# Revit family: HOSPITAIR C 15 bar
name_source: partatom
category: Equipement de génie climatique
revit_build: Autodesk Revit 2018 (Build: 20170223_1515(x64)
units: mm (PartAtom-declared; Revit-internal decimal feet)

## family parameters
Basée sur le plan de construction = Non
Classification = Aucun
Cote de connecteur circulaire = Utiliser le diamètre
Couper avec des vides une fois chargée = Non
Partagée = Non
Point de calcul de pièce = Non
Toujours verticalement = Oui
Type d'élément = Normal

## types (21) — shared parameters
BRANCHEMENT_TERRE = Oui
COS_PHI = 0.9
DESCR_CONDENSAT = Refoulement Condensat; Douille cannelée G1/2"
DIAM_REFOUL_CONDENSAT = 14 mm  [stored 0.0459318 ft]
Debit_refoulement_condensat = 0.0 m³/h
ELEC_ALIM X = Oui
HAUTEUR_CABINE = 2600 mm
LARGEUR_CABINE = 2400 mm
MVX4-5_ASPI_VENT C2 = Non
NBR_POLES = 3
NEUTRE = Oui
TENSION_ALIM = 400 V
Zone de maintenance = Non

## per-type parameters (varying)
- HOSPITAIR C2 - 15 bar - MVX4 (CLIM): C1 LONGUEUR=910 mm  [stored 2.98556 ft]; C1-C2_HAUTEUR=1145 mm; C1-C2_HAUTEUR TROU=300 mm  [stored 0.984252 ft]; C1_LONGUEUR TROU=300 mm  [stored 0.984252 ft]; C2 LONGUEUR=970 mm; C2_LONGUEUR TROU=300 mm  [stored 0.984252 ft]; CLIMATISATION=Oui; DESCR_ALIM_X=Alimentation électrique, 5G4mm²; DESCR_ALIM_Y=Alimentation électrique, 5G1.5mm²; DESCR_REFOULEMENT RESEAU_AIR=Refoulement Réseau Air; 44m3/h; G3/4"FEM; DESCR_RESERVOIR_AIR=Connexion Réservoir Air; G3/4"FEM; DIAM_REFOULEMENT RESEAU_AIR=20 mm  [stored 0.0656168 ft]; DIAM_RESEVOIR_AIR=20 mm  [stored 0.0656168 ft]; DOUBLE_ALIMENTATION=Oui; Debit_refoulement réseau_air=44.0 m³/h; Debit_réservoir_air=44.0 m³/h; ELEC_ALIM Y=Oui; HAUT_CONDENSATS=308 mm  [stored 1.0105 ft]; HAUT_SORTIE_RESEAU=1498 mm; HAUT_SORTIE_RESERV=1216 mm; HAUT_TROU_VENTIL=2041.5 mm; LARG_CONDENSATS=857 mm  [stored 2.81168 ft]; LARG_SORTIE_RESEAU=785 mm; LARG_SORTIE_RESERV=1580 mm; LONGUEUR_CABINE=3500 mm; MVA9_ASPI_VENT C1=Non; MVA9_ASPI_VENT C2=Non; MVB12_C1=Non; MVB12_C2=Non; MVC19-23_ASPI_VENT C1=Non; MVC19-23_ASPI_VENT C2=Non; MVC19-23_C1=Non; MVC19-23_C2=Non; MVX4-5 MVA9_C1=Oui; MVX4-5 MVA9_C2=Oui; MVX4-5_ASPI_VENT C1=Oui; MVX4-5_MVA9_MVB12-16_MVC19-23_VENT=Non; NIVEAU_SONORE(dB(A))=57; POIDS(Kg)=1800 mm; PUISS_APPARENTE_X=9333 VA; PUISS_APPARENTE_Y=4556 VA; PUISS_ELECT_X=8 kW; PUISS_ELECT_Y=4 kW; VENTILATION LONGUEUR=4500 mm; VENTIL_LONGUEUR 1=450 mm  [stored 1.47638 ft]; VENTIL_LONGUEUR 2=3000 mm; VENTIL_TROU 1-2  HAUTEUR=600 mm  [stored 1.9685 ft]; VENTIL_TROU 1-2 HAUTEUR=360 mm  [stored 1.1811 ft]; VENTIL_TROU1 LONGUEUR=600 mm  [stored 1.9685 ft]; VENTIL_TROU2 LONGUEUR=500 mm  [stored 1.64042 ft]
- HOSPITAIR C2 - 15 bar - MVA9 (CLIM): C1 LONGUEUR=1040 mm; C1-C2_HAUTEUR=1286.5 mm; C1-C2_HAUTEUR TROU=300 mm  [stored 0.984252 ft]; C1_LONGUEUR TROU=300 mm  [stored 0.984252 ft]; C2 LONGUEUR=1170 mm; C2_LONGUEUR TROU=300 mm  [stored 0.984252 ft]; CLIMATISATION=Oui; DESCR_ALIM_X=Alimentation électrique, 5G10mm²; DESCR_ALIM_Y=Alimentation électrique, 5G6mm²; DESCR_REFOULEMENT RESEAU_AIR=Refoulement Réseau Air; 100m3/h; G3/4"FEM; DESCR_RESERVOIR_AIR=Connexion Réservoir Air; G3/4"FEM; DIAM_REFOULEMENT RESEAU_AIR=20 mm  [stored 0.0656168 ft]; DIAM_RESEVOIR_AIR=20 mm  [stored 0.0656168 ft]; DOUBLE_ALIMENTATION=Oui; Debit_refoulement réseau_air=100.0 m³/h; Debit_réservoir_air=100.0 m³/h; ELEC_ALIM Y=Oui; HAUT_CONDENSATS=283 mm  [stored 0.928478 ft]; HAUT_SORTIE_RESEAU=1510 mm; HAUT_SORTIE_RESERV=1235 mm; HAUT_TROU_VENTIL=2041.5 mm; LARG_CONDENSATS=804 mm  [stored 2.6378 ft]; LARG_SORTIE_RESEAU=785 mm; LARG_SORTIE_RESERV=1580 mm; LONGUEUR_CABINE=4000 mm; MVA9_ASPI_VENT C1=Oui; MVA9_ASPI_VENT C2=Non; MVB12_C1=Non; MVB12_C2=Non; MVC19-23_ASPI_VENT C1=Non; MVC19-23_ASPI_VENT C2=Non; MVC19-23_C1=Non; MVC19-23_C2=Non; MVX4-5 MVA9_C1=Oui; MVX4-5 MVA9_C2=Oui; MVX4-5_ASPI_VENT C1=Non; MVX4-5_MVA9_MVB12-16_MVC19-23_VENT=Non; NIVEAU_SONORE(dB(A))=58; POIDS(Kg)=2010 mm; PUISS_APPARENTE_X=13222 VA; PUISS_APPARENTE_Y=8444 VA; PUISS_ELECT_X=12 kW; PUISS_ELECT_Y=8 kW; VENTILATION LONGUEUR=4500 mm; VENTIL_LONGUEUR 1=510 mm  [stored 1.67323 ft]; VENTIL_LONGUEUR 2=3000 mm; VENTIL_TROU 1-2  HAUTEUR=700 mm  [stored 2.29659 ft]; VENTIL_TROU 1-2 HAUTEUR=460 mm  [stored 1.50919 ft]; VENTIL_TROU1 LONGUEUR=700 mm  [stored 2.29659 ft]; VENTIL_TROU2 LONGUEUR=700 mm  [stored 2.29659 ft]
- HOSPITAIR C2 - 15 bar - MVB12 (CLIM): C1 LONGUEUR=960 mm; C1-C2_HAUTEUR=1437 mm; C1-C2_HAUTEUR TROU=400 mm  [stored 1.31234 ft]; C1_LONGUEUR TROU=400 mm  [stored 1.31234 ft]; C2 LONGUEUR=1100 mm; C2_LONGUEUR TROU=400 mm  [stored 1.31234 ft]; CLIMATISATION=Oui; DESCR_ALIM_X=Alimentation électrique, 5G16mm²; DESCR_ALIM_Y=Alimentation électrique, 5G10mm²; DESCR_REFOULEMENT RESEAU_AIR=Refoulement Réseau Air; 156m3/h; G3/4"FEM; DESCR_RESERVOIR_AIR=Connexion Réservoir Air; G3/4"FEM; DIAM_REFOULEMENT RESEAU_AIR=20 mm  [stored 0.0656168 ft]; DIAM_RESEVOIR_AIR=20 mm  [stored 0.0656168 ft]; DOUBLE_ALIMENTATION=Oui; Debit_refoulement réseau_air=156.0 m³/h; Debit_réservoir_air=156.0 m³/h; ELEC_ALIM Y=Oui; HAUT_CONDENSATS=310 mm  [stored 1.01706 ft]; HAUT_SORTIE_RESEAU=1629 mm; HAUT_SORTIE_RESERV=1261 mm; HAUT_TROU_VENTIL=2041.5 mm; LARG_CONDENSATS=1100 mm; LARG_SORTIE_RESEAU=785 mm; LARG_SORTIE_RESERV=1612 mm; LONGUEUR_CABINE=4000 mm; MVA9_ASPI_VENT C1=Oui; MVA9_ASPI_VENT C2=Oui; MVB12_C1=Oui; MVB12_C2=Oui; MVC19-23_ASPI_VENT C1=Non; MVC19-23_ASPI_VENT C2=Non; MVC19-23_C1=Non; MVC19-23_C2=Non; MVX4-5 MVA9_C1=Non; MVX4-5 MVA9_C2=Non; MVX4-5_ASPI_VENT C1=Non; MVX4-5_MVA9_MVB12-16_MVC19-23_VENT=Non; NIVEAU_SONORE(dB(A))=58; POIDS(Kg)=2300 mm; PUISS_APPARENTE_X=17111 VA; PUISS_APPARENTE_Y=12333 VA; PUISS_ELECT_X=15 kW; PUISS_ELECT_Y=11 kW; VENTILATION LONGUEUR=4500 mm; VENTIL_LONGUEUR 1=250 mm  [stored 0.82021 ft]; VENTIL_LONGUEUR 2=1290 mm; VENTIL_TROU 1-2  HAUTEUR=700 mm  [stored 2.29659 ft]; VENTIL_TROU 1-2 HAUTEUR=360 mm  [stored 1.1811 ft]; VENTIL_TROU1 LONGUEUR=700 mm  [stored 2.29659 ft]; VENTIL_TROU2 LONGUEUR=700 mm  [stored 2.29659 ft]
- HOSPITAIR C2 - 15 bar - MVB16 (CLIM): C1 LONGUEUR=1060 mm; C1-C2_HAUTEUR=1437 mm; C1-C2_HAUTEUR TROU=400 mm  [stored 1.31234 ft]; C1_LONGUEUR TROU=400 mm  [stored 1.31234 ft]; C2 LONGUEUR=1590 mm; C2_LONGUEUR TROU=400 mm  [stored 1.31234 ft]; CLIMATISATION=Oui; DESCR_ALIM_X=Alimentation électrique, 5G16mm²; DESCR_ALIM_Y=Alimentation électrique, 5G16mm²; DESCR_REFOULEMENT RESEAU_AIR=Refoulement Réseau Air; 204m3/h; G3/4"FEM; DESCR_RESERVOIR_AIR=Connexion Réservoir Air; G3/4"FEM; DIAM_REFOULEMENT RESEAU_AIR=20 mm  [stored 0.0656168 ft]; DIAM_RESEVOIR_AIR=20 mm  [stored 0.0656168 ft]; DOUBLE_ALIMENTATION=Oui; Debit_refoulement réseau_air=204.0 m³/h; Debit_réservoir_air=204.0 m³/h; ELEC_ALIM Y=Oui; HAUT_CONDENSATS=310 mm  [stored 1.01706 ft]; HAUT_SORTIE_RESEAU=1629 mm; HAUT_SORTIE_RESERV=1261 mm; HAUT_TROU_VENTIL=2041.5 mm; LARG_CONDENSATS=800 mm  [stored 2.62467 ft]; LARG_SORTIE_RESEAU=785 mm; LARG_SORTIE_RESERV=1612 mm; LONGUEUR_CABINE=4000 mm; MVA9_ASPI_VENT C1=Oui; MVA9_ASPI_VENT C2=Oui; MVB12_C1=Oui; MVB12_C2=Oui; MVC19-23_ASPI_VENT C1=Non; MVC19-23_ASPI_VENT C2=Non; MVC19-23_C1=Non; MVC19-23_C2=Non; MVX4-5 MVA9_C1=Non; MVX4-5 MVA9_C2=Non; MVX4-5_ASPI_VENT C1=Non; MVX4-5_MVA9_MVB12-16_MVC19-23_VENT=Non; NIVEAU_SONORE(dB(A))=62; POIDS(Kg)=2600 mm; PUISS_APPARENTE_X=21556 VA; PUISS_APPARENTE_Y=16778 VA; PUISS_ELECT_X=19 kW; PUISS_ELECT_Y=15 kW; VENTILATION LONGUEUR=4500 mm; VENTIL_LONGUEUR 1=250 mm  [stored 0.82021 ft]; VENTIL_LONGUEUR 2=1290 mm; VENTIL_TROU 1-2  HAUTEUR=700 mm  [stored 2.29659 ft]; VENTIL_TROU 1-2 HAUTEUR=360 mm  [stored 1.1811 ft]; VENTIL_TROU1 LONGUEUR=700 mm  [stored 2.29659 ft]; VENTIL_TROU2 LONGUEUR=700 mm  [stored 2.29659 ft]
- HOSPITAIR C2 - 15 bar - MVC19 (CLIM): C1 LONGUEUR=1017 mm; C1-C2_HAUTEUR=1728 mm; C1-C2_HAUTEUR TROU=500 mm  [stored 1.64042 ft]; C1_LONGUEUR TROU=500 mm  [stored 1.64042 ft]; C2 LONGUEUR=1200 mm; C2_LONGUEUR TROU=500 mm  [stored 1.64042 ft]; CLIMATISATION=Oui; DESCR_ALIM_X=Alimentation électrique, 5G25mm²; DESCR_ALIM_Y=Alimentation électrique, 5G16mm²; DESCR_REFOULEMENT RESEAU_AIR=Refoulement Réseau Air; 300m3/h; G3/4"FEM; DESCR_RESERVOIR_AIR=Connexion Réservoir Air; G3/4"FEM; DIAM_REFOULEMENT RESEAU_AIR=20 mm  [stored 0.0656168 ft]; DIAM_RESEVOIR_AIR=20 mm  [stored 0.0656168 ft]; DOUBLE_ALIMENTATION=Oui; Debit_refoulement réseau_air=300.0 m³/h; Debit_réservoir_air=300.0 m³/h; ELEC_ALIM Y=Oui; HAUT_CONDENSATS=310 mm  [stored 1.01706 ft]; HAUT_SORTIE_RESEAU=1629 mm; HAUT_SORTIE_RESERV=1254 mm; HAUT_TROU_VENTIL=2041.5 mm; LARG_CONDENSATS=795 mm  [stored 2.60827 ft]; LARG_SORTIE_RESEAU=860 mm  [stored 2.82152 ft]; LARG_SORTIE_RESERV=1705 mm; LONGUEUR_CABINE=4300 mm; MVA9_ASPI_VENT C1=Non; MVA9_ASPI_VENT C2=Non; MVB12_C1=Non; MVB12_C2=Non; MVC19-23_ASPI_VENT C1=Oui; MVC19-23_ASPI_VENT C2=Oui; MVC19-23_C1=Oui; MVC19-23_C2=Oui; MVX4-5 MVA9_C1=Non; MVX4-5 MVA9_C2=Non; MVX4-5_ASPI_VENT C1=Non; MVX4-5_MVA9_MVB12-16_MVC19-23_VENT=Non; NIVEAU_SONORE(dB(A))=62; POIDS(Kg)=2750 mm; PUISS_APPARENTE_X=25444 VA; PUISS_APPARENTE_Y=20667 VA; PUISS_ELECT_X=23 kW; PUISS_ELECT_Y=19 kW; VENTILATION LONGUEUR=4500 mm; VENTIL_LONGUEUR 1=780 mm  [stored 2.55906 ft]; VENTIL_LONGUEUR 2=880 mm  [stored 2.88714 ft]; VENTIL_TROU 1-2  HAUTEUR=800 mm  [stored 2.62467 ft]; VENTIL_TROU 1-2 HAUTEUR=360 mm  [stored 1.1811 ft]; VENTIL_TROU1 LONGUEUR=800 mm  [stored 2.62467 ft]; VENTIL_TROU2 LONGUEUR=800 mm  [stored 2.62467 ft]
- HOSPITAIR C2 - 15 bar - MVC23 (CLIM): C1 LONGUEUR=1017 mm; C1-C2_HAUTEUR=1728 mm; C1-C2_HAUTEUR TROU=500 mm  [stored 1.64042 ft]; C1_LONGUEUR TROU=500 mm  [stored 1.64042 ft]; C2 LONGUEUR=1200 mm; C2_LONGUEUR TROU=500 mm  [stored 1.64042 ft]; CLIMATISATION=Oui; DESCR_ALIM_X=Alimentation électrique, 5G25mm²; DESCR_ALIM_Y=Alimentation électrique, 5G25mm²; DESCR_REFOULEMENT RESEAU_AIR=Refoulement Réseau Air; 348m3/h; G3/4"FEM; DESCR_RESERVOIR_AIR=Connexion Réservoir Air; G3/4"FEM; DIAM_REFOULEMENT RESEAU_AIR=20 mm  [stored 0.0656168 ft]; DIAM_RESEVOIR_AIR=20 mm  [stored 0.0656168 ft]; DOUBLE_ALIMENTATION=Oui; Debit_refoulement réseau_air=348.0 m³/h; Debit_réservoir_air=348.0 m³/h; ELEC_ALIM Y=Oui; HAUT_CONDENSATS=310 mm  [stored 1.01706 ft]; HAUT_SORTIE_RESEAU=1629 mm; HAUT_SORTIE_RESERV=1255 mm; HAUT_TROU_VENTIL=2041.5 mm; LARG_CONDENSATS=800 mm  [stored 2.62467 ft]; LARG_SORTIE_RESEAU=785 mm; LARG_SORTIE_RESERV=1665 mm; LONGUEUR_CABINE=4300 mm; MVA9_ASPI_VENT C1=Non; MVA9_ASPI_VENT C2=Non; MVB12_C1=Non; MVB12_C2=Non; MVC19-23_ASPI_VENT C1=Oui; MVC19-23_ASPI_VENT C2=Oui; MVC19-23_C1=Oui; MVC19-23_C2=Oui; MVX4-5 MVA9_C1=Non; MVX4-5 MVA9_C2=Non; MVX4-5_ASPI_VENT C1=Non; MVX4-5_MVA9_MVB12-16_MVC19-23_VENT=Non; NIVEAU_SONORE(dB(A))=63; POIDS(Kg)=3290 mm; PUISS_APPARENTE_X=29333 VA; PUISS_APPARENTE_Y=24556 VA; PUISS_ELECT_X=26 kW; PUISS_ELECT_Y=22 kW; VENTILATION LONGUEUR=4500 mm; VENTIL_LONGUEUR 1=780 mm  [stored 2.55906 ft]; VENTIL_LONGUEUR 2=880 mm  [stored 2.88714 ft]; VENTIL_TROU 1-2  HAUTEUR=800 mm  [stored 2.62467 ft]; VENTIL_TROU 1-2 HAUTEUR=360 mm  [stored 1.1811 ft]; VENTIL_TROU1 LONGUEUR=800 mm  [stored 2.62467 ft]; VENTIL_TROU2 LONGUEUR=800 mm  [stored 2.62467 ft]
- HOSPITAIR C2 - 15 bar - MVX4 (NO CLIM): C1 LONGUEUR=910 mm  [stored 2.98556 ft]; C1-C2_HAUTEUR=1145 mm; C1-C2_HAUTEUR TROU=300 mm  [stored 0.984252 ft]; C1_LONGUEUR TROU=300 mm  [stored 0.984252 ft]; C2 LONGUEUR=970 mm; C2_LONGUEUR TROU=300 mm  [stored 0.984252 ft]; CLIMATISATION=Non; DESCR_ALIM_X=Alimentation électrique, 5G2.5mm²; DESCR_ALIM_Y=Alimentation électrique, 5G1.5mm²; DESCR_REFOULEMENT RESEAU_AIR=Refoulement Réseau Air; 44m3/h; G3/4"FEM; DESCR_RESERVOIR_AIR=Connexion Réservoir Air; G3/4"FEM; DIAM_REFOULEMENT RESEAU_AIR=20 mm  [stored 0.0656168 ft]; DIAM_RESEVOIR_AIR=20 mm  [stored 0.0656168 ft]; DOUBLE_ALIMENTATION=Oui; Debit_refoulement réseau_air=44.0 m³/h; Debit_réservoir_air=44.0 m³/h; ELEC_ALIM Y=Oui; HAUT_CONDENSATS=310 mm  [stored 1.01706 ft]; HAUT_SORTIE_RESEAU=1510 mm; HAUT_SORTIE_RESERV=1200 mm; HAUT_TROU_VENTIL=2000 mm; LARG_CONDENSATS=1100 mm; LARG_SORTIE_RESEAU=785 mm; LARG_SORTIE_RESERV=1580 mm; LONGUEUR_CABINE=3500 mm; MVA9_ASPI_VENT C1=Non; MVA9_ASPI_VENT C2=Non; MVB12_C1=Non; MVB12_C2=Non; MVC19-23_ASPI_VENT C1=Non; MVC19-23_ASPI_VENT C2=Non; MVC19-23_C1=Non; MVC19-23_C2=Non; MVX4-5 MVA9_C1=Oui; MVX4-5 MVA9_C2=Oui; MVX4-5_ASPI_VENT C1=Oui; MVX4-5_MVA9_MVB12-16_MVC19-23_VENT=Oui; NIVEAU_SONORE(dB(A))=57; POIDS(Kg)=1800 mm; PUISS_APPARENTE_X=7444 VA; PUISS_APPARENTE_Y=4556 VA; PUISS_ELECT_X=7 kW; PUISS_ELECT_Y=4 kW; VENTILATION LONGUEUR=2940 mm; VENTIL_LONGUEUR 1=450 mm  [stored 1.47638 ft]; VENTIL_LONGUEUR 2=3000 mm; VENTIL_TROU 1-2  HAUTEUR=500 mm  [stored 1.64042 ft]; VENTIL_TROU 1-2 HAUTEUR=360 mm  [stored 1.1811 ft]; VENTIL_TROU1 LONGUEUR=600 mm  [stored 1.9685 ft]; VENTIL_TROU2 LONGUEUR=500 mm  [stored 1.64042 ft]
- HOSPITAIR C2 - 15 bar - MVA9 (NO CLIM): C1 LONGUEUR=1040 mm; C1-C2_HAUTEUR=1286.5 mm; C1-C2_HAUTEUR TROU=300 mm  [stored 0.984252 ft]; C1_LONGUEUR TROU=300 mm  [stored 0.984252 ft]; C2 LONGUEUR=1170 mm; C2_LONGUEUR TROU=300 mm  [stored 0.984252 ft]; CLIMATISATION=Non; DESCR_ALIM_X=Alimentation électrique, 5G6mm²; DESCR_ALIM_Y=Alimentation électrique, 5G6mm²; DESCR_REFOULEMENT RESEAU_AIR=Refoulement Réseau Air; 100m3/h; G3/4"FEM; DESCR_RESERVOIR_AIR=Connexion Réservoir Air; G3/4"FEM; DIAM_REFOULEMENT RESEAU_AIR=20 mm  [stored 0.0656168 ft]; DIAM_RESEVOIR_AIR=20 mm  [stored 0.0656168 ft]; DOUBLE_ALIMENTATION=Oui; Debit_refoulement réseau_air=100.0 m³/h; Debit_réservoir_air=100.0 m³/h; ELEC_ALIM Y=Oui; HAUT_CONDENSATS=310 mm  [stored 1.01706 ft]; HAUT_SORTIE_RESEAU=1510 mm; HAUT_SORTIE_RESERV=1210 mm; HAUT_TROU_VENTIL=2000 mm; LARG_CONDENSATS=1100 mm; LARG_SORTIE_RESEAU=785 mm; LARG_SORTIE_RESERV=1580 mm; LONGUEUR_CABINE=4000 mm; MVA9_ASPI_VENT C1=Oui; MVA9_ASPI_VENT C2=Non; MVB12_C1=Non; MVB12_C2=Non; MVC19-23_ASPI_VENT C1=Non; MVC19-23_ASPI_VENT C2=Non; MVC19-23_C1=Non; MVC19-23_C2=Non; MVX4-5 MVA9_C1=Oui; MVX4-5 MVA9_C2=Oui; MVX4-5_ASPI_VENT C1=Non; MVX4-5_MVA9_MVB12-16_MVC19-23_VENT=Oui; NIVEAU_SONORE(dB(A))=58; POIDS(Kg)=2010 mm; PUISS_APPARENTE_X=11333 VA; PUISS_APPARENTE_Y=8444 VA; PUISS_ELECT_X=10 kW; PUISS_ELECT_Y=8 kW; VENTILATION LONGUEUR=3500 mm; VENTIL_LONGUEUR 1=510 mm  [stored 1.67323 ft]; VENTIL_LONGUEUR 2=3000 mm; VENTIL_TROU 1-2  HAUTEUR=700 mm  [stored 2.29659 ft]; VENTIL_TROU 1-2 HAUTEUR=460 mm  [stored 1.50919 ft]; VENTIL_TROU1 LONGUEUR=700 mm  [stored 2.29659 ft]; VENTIL_TROU2 LONGUEUR=700 mm  [stored 2.29659 ft]
- HOSPITAIR C2 - 15 bar - MVB12 (NO CLIM): C1 LONGUEUR=960 mm; C1-C2_HAUTEUR=1437 mm; C1-C2_HAUTEUR TROU=400 mm  [stored 1.31234 ft]; C1_LONGUEUR TROU=400 mm  [stored 1.31234 ft]; C2 LONGUEUR=1100 mm; C2_LONGUEUR TROU=400 mm  [stored 1.31234 ft]; CLIMATISATION=Non; DESCR_ALIM_X=Alimentation électrique, 5G16mm²; DESCR_ALIM_Y=Alimentation électrique, 5G10mm²; DESCR_REFOULEMENT RESEAU_AIR=Refoulement Réseau Air; 156m3/h; G3/4"FEM; DESCR_RESERVOIR_AIR=Connexion Réservoir Air; G3/4"FEM; DIAM_REFOULEMENT RESEAU_AIR=20 mm  [stored 0.0656168 ft]; DIAM_RESEVOIR_AIR=20 mm  [stored 0.0656168 ft]; DOUBLE_ALIMENTATION=Oui; Debit_refoulement réseau_air=156.0 m³/h; Debit_réservoir_air=156.0 m³/h; ELEC_ALIM Y=Oui; HAUT_CONDENSATS=310 mm  [stored 1.01706 ft]; HAUT_SORTIE_RESEAU=1637 mm; HAUT_SORTIE_RESERV=1313 mm; HAUT_TROU_VENTIL=2000 mm; LARG_CONDENSATS=760 mm; LARG_SORTIE_RESEAU=833 mm  [stored 2.73294 ft]; LARG_SORTIE_RESERV=1660 mm; LONGUEUR_CABINE=4000 mm; MVA9_ASPI_VENT C1=Oui; MVA9_ASPI_VENT C2=Oui; MVB12_C1=Oui; MVB12_C2=Oui; MVC19-23_ASPI_VENT C1=Non; MVC19-23_ASPI_VENT C2=Non; MVC19-23_C1=Non; MVC19-23_C2=Non; MVX4-5 MVA9_C1=Non; MVX4-5 MVA9_C2=Non; MVX4-5_ASPI_VENT C1=Non; MVX4-5_MVA9_MVB12-16_MVC19-23_VENT=Oui; NIVEAU_SONORE(dB(A))=58; POIDS(Kg)=2300 mm; PUISS_APPARENTE_X=15222 VA; PUISS_APPARENTE_Y=12333 VA; PUISS_ELECT_X=14 kW; PUISS_ELECT_Y=11 kW; VENTILATION LONGUEUR=3500 mm; VENTIL_LONGUEUR 1=250 mm  [stored 0.82021 ft]; VENTIL_LONGUEUR 2=1290 mm; VENTIL_TROU 1-2  HAUTEUR=700 mm  [stored 2.29659 ft]; VENTIL_TROU 1-2 HAUTEUR=360 mm  [stored 1.1811 ft]; VENTIL_TROU1 LONGUEUR=700 mm  [stored 2.29659 ft]; VENTIL_TROU2 LONGUEUR=700 mm  [stored 2.29659 ft]
- HOSPITAIR C2 - 15 bar - MVB16 (NO CLIM): C1 LONGUEUR=960 mm; C1-C2_HAUTEUR=1437 mm; C1-C2_HAUTEUR TROU=400 mm  [stored 1.31234 ft]; C1_LONGUEUR TROU=400 mm  [stored 1.31234 ft]; C2 LONGUEUR=1100 mm; C2_LONGUEUR TROU=400 mm  [stored 1.31234 ft]; CLIMATISATION=Non; DESCR_ALIM_X=Alimentation électrique, 5G16mm²; DESCR_ALIM_Y=Alimentation électrique, 5G16mm²; DESCR_REFOULEMENT RESEAU_AIR=Refoulement Réseau Air; 204m3/h; G3/4"FEM; DESCR_RESERVOIR_AIR=Connexion Réservoir Air; G3/4"FEM; DIAM_REFOULEMENT RESEAU_AIR=20 mm  [stored 0.0656168 ft]; DIAM_RESEVOIR_AIR=20 mm  [stored 0.0656168 ft]; DOUBLE_ALIMENTATION=Oui; Debit_refoulement réseau_air=204.0 m³/h; Debit_réservoir_air=204.0 m³/h; ELEC_ALIM Y=Oui; HAUT_CONDENSATS=310 mm  [stored 1.01706 ft]; HAUT_SORTIE_RESEAU=1629 mm; HAUT_SORTIE_RESERV=1261 mm; HAUT_TROU_VENTIL=2000 mm; LARG_CONDENSATS=800 mm  [stored 2.62467 ft]; LARG_SORTIE_RESEAU=785 mm; LARG_SORTIE_RESERV=1612 mm; LONGUEUR_CABINE=4000 mm; MVA9_ASPI_VENT C1=Oui; MVA9_ASPI_VENT C2=Oui; MVB12_C1=Oui; MVB12_C2=Oui; MVC19-23_ASPI_VENT C1=Non; MVC19-23_ASPI_VENT C2=Non; MVC19-23_C1=Non; MVC19-23_C2=Non; MVX4-5 MVA9_C1=Non; MVX4-5 MVA9_C2=Non; MVX4-5_ASPI_VENT C1=Non; MVX4-5_MVA9_MVB12-16_MVC19-23_VENT=Oui; NIVEAU_SONORE(dB(A))=62; POIDS(Kg)=2600 mm; PUISS_APPARENTE_X=19667 VA; PUISS_APPARENTE_Y=16778 VA; PUISS_ELECT_X=18 kW; PUISS_ELECT_Y=15 kW; VENTILATION LONGUEUR=3500 mm; VENTIL_LONGUEUR 1=250 mm  [stored 0.82021 ft]; VENTIL_LONGUEUR 2=1290 mm; VENTIL_TROU 1-2  HAUTEUR=700 mm  [stored 2.29659 ft]; VENTIL_TROU 1-2 HAUTEUR=360 mm  [stored 1.1811 ft]; VENTIL_TROU1 LONGUEUR=700 mm  [stored 2.29659 ft]; VENTIL_TROU2 LONGUEUR=700 mm  [stored 2.29659 ft]
- HOSPITAIR C2 - 15 bar - MVC19 (NO CLIM): C1 LONGUEUR=1017 mm; C1-C2_HAUTEUR=1721 mm; C1-C2_HAUTEUR TROU=500 mm  [stored 1.64042 ft]; C1_LONGUEUR TROU=500 mm  [stored 1.64042 ft]; C2 LONGUEUR=1200 mm; C2_LONGUEUR TROU=500 mm  [stored 1.64042 ft]; CLIMATISATION=Non; DESCR_ALIM_X=Alimentation électrique, 5G25mm²; DESCR_ALIM_Y=Alimentation électrique, 5G16mm²; DESCR_REFOULEMENT RESEAU_AIR=Refoulement Réseau Air; 300m3/h; G3/4"FEM; DESCR_RESERVOIR_AIR=Connexion Réservoir Air; G3/4"FEM; DIAM_REFOULEMENT RESEAU_AIR=20 mm  [stored 0.0656168 ft]; DIAM_RESEVOIR_AIR=20 mm  [stored 0.0656168 ft]; DOUBLE_ALIMENTATION=Oui; Debit_refoulement réseau_air=300.0 m³/h; Debit_réservoir_air=300.0 m³/h; ELEC_ALIM Y=Oui; HAUT_CONDENSATS=310 mm  [stored 1.01706 ft]; HAUT_SORTIE_RESEAU=1617 mm; HAUT_SORTIE_RESERV=1293 mm; HAUT_TROU_VENTIL=2000 mm; LARG_CONDENSATS=760 mm; LARG_SORTIE_RESEAU=780 mm  [stored 2.55906 ft]; LARG_SORTIE_RESERV=1660 mm; LONGUEUR_CABINE=4300 mm; MVA9_ASPI_VENT C1=Non; MVA9_ASPI_VENT C2=Non; MVB12_C1=Non; MVB12_C2=Non; MVC19-23_ASPI_VENT C1=Oui; MVC19-23_ASPI_VENT C2=Oui; MVC19-23_C1=Oui; MVC19-23_C2=Oui; MVX4-5 MVA9_C1=Non; MVX4-5 MVA9_C2=Non; MVX4-5_ASPI_VENT C1=Non; MVX4-5_MVA9_MVB12-16_MVC19-23_VENT=Oui; NIVEAU_SONORE(dB(A))=62; POIDS(Kg)=2750 mm; PUISS_APPARENTE_X=23556 VA; PUISS_APPARENTE_Y=20667 VA; PUISS_ELECT_X=21 kW; PUISS_ELECT_Y=19 kW; VENTILATION LONGUEUR=3850 mm; VENTIL_LONGUEUR 1=780 mm  [stored 2.55906 ft]; VENTIL_LONGUEUR 2=860 mm  [stored 2.82152 ft]; VENTIL_TROU 1-2  HAUTEUR=800 mm  [stored 2.62467 ft]; VENTIL_TROU 1-2 HAUTEUR=360 mm  [stored 1.1811 ft]; VENTIL_TROU1 LONGUEUR=800 mm  [stored 2.62467 ft]; VENTIL_TROU2 LONGUEUR=800 mm  [stored 2.62467 ft]
- HOSPITAIR C2 - 15 bar - MVC23 (NO CLIM): C1 LONGUEUR=1017 mm; C1-C2_HAUTEUR=1721 mm; C1-C2_HAUTEUR TROU=500 mm  [stored 1.64042 ft]; C1_LONGUEUR TROU=500 mm  [stored 1.64042 ft]; C2 LONGUEUR=1200 mm; C2_LONGUEUR TROU=500 mm  [stored 1.64042 ft]; CLIMATISATION=Non; DESCR_ALIM_X=Alimentation électrique, 5G25mm²; DESCR_ALIM_Y=Alimentation électrique, 5G25mm²; DESCR_REFOULEMENT RESEAU_AIR=Refoulement Réseau Air; 348m3/h; G3/4"FEM; DESCR_RESERVOIR_AIR=Connexion Réservoir Air; G3/4"FEM; DIAM_REFOULEMENT RESEAU_AIR=20 mm  [stored 0.0656168 ft]; DIAM_RESEVOIR_AIR=20 mm  [stored 0.0656168 ft]; DOUBLE_ALIMENTATION=Oui; Debit_refoulement réseau_air=348.0 m³/h; Debit_réservoir_air=348.0 m³/h; ELEC_ALIM Y=Oui; HAUT_CONDENSATS=310 mm  [stored 1.01706 ft]; HAUT_SORTIE_RESEAU=1617 mm; HAUT_SORTIE_RESERV=1293 mm; HAUT_TROU_VENTIL=2000 mm; LARG_CONDENSATS=760 mm; LARG_SORTIE_RESEAU=780 mm  [stored 2.55906 ft]; LARG_SORTIE_RESERV=1660 mm; LONGUEUR_CABINE=4300 mm; MVA9_ASPI_VENT C1=Non; MVA9_ASPI_VENT C2=Non; MVB12_C1=Non; MVB12_C2=Non; MVC19-23_ASPI_VENT C1=Oui; MVC19-23_ASPI_VENT C2=Oui; MVC19-23_C1=Oui; MVC19-23_C2=Oui; MVX4-5 MVA9_C1=Non; MVX4-5 MVA9_C2=Non; MVX4-5_ASPI_VENT C1=Non; MVX4-5_MVA9_MVB12-16_MVC19-23_VENT=Oui; NIVEAU_SONORE(dB(A))=63; POIDS(Kg)=3290 mm; PUISS_APPARENTE_X=27444 VA; PUISS_APPARENTE_Y=24556 VA; PUISS_ELECT_X=25 kW; PUISS_ELECT_Y=22 kW; VENTILATION LONGUEUR=3740 mm; VENTIL_LONGUEUR 1=780 mm  [stored 2.55906 ft]; VENTIL_LONGUEUR 2=860 mm  [stored 2.82152 ft]; VENTIL_TROU 1-2  HAUTEUR=800 mm  [stored 2.62467 ft]; VENTIL_TROU 1-2 HAUTEUR=360 mm  [stored 1.1811 ft]; VENTIL_TROU1 LONGUEUR=800 mm  [stored 2.62467 ft]; VENTIL_TROU2 LONGUEUR=800 mm  [stored 2.62467 ft]
- HOSPITAIR C1 - 15 bar - MVX4 (NO CLIM): C1 LONGUEUR=905 mm  [stored 2.96916 ft]; C1-C2_HAUTEUR=1146.5 mm; C1-C2_HAUTEUR TROU=300 mm  [stored 0.984252 ft]; C1_LONGUEUR TROU=300 mm  [stored 0.984252 ft]; C2 LONGUEUR=1200 mm; C2_LONGUEUR TROU=300 mm  [stored 0.984252 ft]; CLIMATISATION=Non; DESCR_ALIM_X=Alimentation électrique, 5G2.5mm²; DESCR_ALIM_Y=NE PAS UTILLISER; DESCR_REFOULEMENT RESEAU_AIR=Refoulement Réseau Air; 22m3/h; G1/2"FEM; DESCR_RESERVOIR_AIR=Connexion Réservoir Air; G1/2"FEM; DIAM_REFOULEMENT RESEAU_AIR=15 mm  [stored 0.0492126 ft]; DIAM_RESEVOIR_AIR=15 mm  [stored 0.0492126 ft]; DOUBLE_ALIMENTATION=Non; Debit_refoulement réseau_air=22.0 m³/h; Debit_réservoir_air=22.0 m³/h; ELEC_ALIM Y=Non; HAUT_CONDENSATS=310 mm  [stored 1.01706 ft]; HAUT_SORTIE_RESEAU=1608 mm; HAUT_SORTIE_RESERV=1260 mm; HAUT_TROU_VENTIL=2041.5 mm; LARG_CONDENSATS=785 mm; LARG_SORTIE_RESEAU=775 mm  [stored 2.54265 ft]; LARG_SORTIE_RESERV=1457 mm; LONGUEUR_CABINE=2200 mm; MVA9_ASPI_VENT C1=Non; MVA9_ASPI_VENT C2=Non; MVB12_C1=Non; MVB12_C2=Non; MVC19-23_ASPI_VENT C1=Non; MVC19-23_ASPI_VENT C2=Non; MVC19-23_C1=Non; MVC19-23_C2=Non; MVX4-5 MVA9_C1=Oui; MVX4-5 MVA9_C2=Non; MVX4-5_ASPI_VENT C1=Oui; MVX4-5_MVA9_MVB12-16_MVC19-23_VENT=Oui; NIVEAU_SONORE(dB(A))=57; POIDS(Kg)=1050 mm; PUISS_APPARENTE_X=7444 VA; PUISS_APPARENTE_Y=0 VA; PUISS_ELECT_X=7 kW; PUISS_ELECT_Y=0 kW; VENTILATION LONGUEUR=1595 mm; VENTIL_LONGUEUR 1=360 mm  [stored 1.1811 ft]; VENTIL_LONGUEUR 2=2000 mm; VENTIL_TROU 1-2  HAUTEUR=500 mm  [stored 1.64042 ft]; VENTIL_TROU 1-2 HAUTEUR=360 mm  [stored 1.1811 ft]; VENTIL_TROU1 LONGUEUR=500 mm  [stored 1.64042 ft]; VENTIL_TROU2 LONGUEUR=500 mm  [stored 1.64042 ft]
- HOSPITAIR C1 - 15 bar - MVA9 (NO CLIM): C1 LONGUEUR=1045 mm; C1-C2_HAUTEUR=1286.5 mm; C1-C2_HAUTEUR TROU=300 mm  [stored 0.984252 ft]; C1_LONGUEUR TROU=300 mm  [stored 0.984252 ft]; C2 LONGUEUR=1300 mm; C2_LONGUEUR TROU=300 mm  [stored 0.984252 ft]; CLIMATISATION=Non; DESCR_ALIM_X=Alimentation électrique, 5G6mm²; DESCR_ALIM_Y=NE PAS UTILLISER; DESCR_REFOULEMENT RESEAU_AIR=Refoulement Réseau Air; 50m3/h; G1/2"FEM; DESCR_RESERVOIR_AIR=Connexion Réservoir Air; G1/2"FEM; DIAM_REFOULEMENT RESEAU_AIR=15 mm  [stored 0.0492126 ft]; DIAM_RESEVOIR_AIR=15 mm  [stored 0.0492126 ft]; DOUBLE_ALIMENTATION=Non; Debit_refoulement réseau_air=50.0 m³/h; Debit_réservoir_air=50.0 m³/h; ELEC_ALIM Y=Non; HAUT_CONDENSATS=388 mm  [stored 1.27297 ft]; HAUT_SORTIE_RESEAU=1517 mm; HAUT_SORTIE_RESERV=1224 mm; HAUT_TROU_VENTIL=2041.5 mm; LARG_CONDENSATS=716 mm  [stored 2.34908 ft]; LARG_SORTIE_RESEAU=798 mm  [stored 2.61811 ft]; LARG_SORTIE_RESERV=1501 mm; LONGUEUR_CABINE=2500 mm; MVA9_ASPI_VENT C1=Oui; MVA9_ASPI_VENT C2=Non; MVB12_C1=Non; MVB12_C2=Non; MVC19-23_ASPI_VENT C1=Non; MVC19-23_ASPI_VENT C2=Non; MVC19-23_C1=Non; MVC19-23_C2=Non; MVX4-5 MVA9_C1=Oui; MVX4-5 MVA9_C2=Non; MVX4-5_ASPI_VENT C1=Non; MVX4-5_MVA9_MVB12-16_MVC19-23_VENT=Oui; NIVEAU_SONORE(dB(A))=58; POIDS(Kg)=1100 mm; PUISS_APPARENTE_X=11333 VA; PUISS_APPARENTE_Y=0 VA; PUISS_ELECT_X=10 kW; PUISS_ELECT_Y=0 kW; VENTILATION LONGUEUR=1895 mm; VENTIL_LONGUEUR 1=360 mm  [stored 1.1811 ft]; VENTIL_LONGUEUR 2=2000 mm; VENTIL_TROU 1-2  HAUTEUR=700 mm  [stored 2.29659 ft]; VENTIL_TROU 1-2 HAUTEUR=360 mm  [stored 1.1811 ft]; VENTIL_TROU1 LONGUEUR=700 mm  [stored 2.29659 ft]; VENTIL_TROU2 LONGUEUR=700 mm  [stored 2.29659 ft]
- HOSPITAIR C1 - 15 bar - MVB12 (NO CLIM): C1 LONGUEUR=955 mm  [stored 3.1332 ft]; C1-C2_HAUTEUR=1430 mm; C1-C2_HAUTEUR TROU=400 mm  [stored 1.31234 ft]; C1_LONGUEUR TROU=400 mm  [stored 1.31234 ft]; C2 LONGUEUR=1500 mm; C2_LONGUEUR TROU=400 mm  [stored 1.31234 ft]; CLIMATISATION=Non; DESCR_ALIM_X=Alimentation électrique, 5G16mm²; DESCR_ALIM_Y=NE PAS UTILLISER; DESCR_REFOULEMENT RESEAU_AIR=Refoulement Réseau Air; 78m3/h; G1/2"FEM; DESCR_RESERVOIR_AIR=Connexion Réservoir Air; G1/2"FEM; DIAM_REFOULEMENT RESEAU_AIR=15 mm  [stored 0.0492126 ft]; DIAM_RESEVOIR_AIR=15 mm  [stored 0.0492126 ft]; DOUBLE_ALIMENTATION=Non; Debit_refoulement réseau_air=78.0 m³/h; Debit_réservoir_air=78.0 m³/h; ELEC_ALIM Y=Non; HAUT_CONDENSATS=391 mm; HAUT_SORTIE_RESEAU=1509 mm; HAUT_SORTIE_RESERV=1184 mm; HAUT_TROU_VENTIL=1900 mm; LARG_CONDENSATS=722 mm  [stored 2.36877 ft]; LARG_SORTIE_RESEAU=789 mm  [stored 2.58858 ft]; LARG_SORTIE_RESERV=1492 mm; LONGUEUR_CABINE=2500 mm; MVA9_ASPI_VENT C1=Oui; MVA9_ASPI_VENT C2=Non; MVB12_C1=Oui; MVB12_C2=Non; MVC19-23_ASPI_VENT C1=Non; MVC19-23_ASPI_VENT C2=Non; MVC19-23_C1=Non; MVC19-23_C2=Non; MVX4-5 MVA9_C1=Non; MVX4-5 MVA9_C2=Non; MVX4-5_ASPI_VENT C1=Non; MVX4-5_MVA9_MVB12-16_MVC19-23_VENT=Oui; NIVEAU_SONORE(dB(A))=58; POIDS(Kg)=1300 mm; PUISS_APPARENTE_X=15222 VA; PUISS_APPARENTE_Y=0 VA; PUISS_ELECT_X=14 kW; PUISS_ELECT_Y=0 kW; VENTILATION LONGUEUR=1695 mm; VENTIL_LONGUEUR 1=360 mm  [stored 1.1811 ft]; VENTIL_LONGUEUR 2=2000 mm; VENTIL_TROU 1-2  HAUTEUR=700 mm  [stored 2.29659 ft]; VENTIL_TROU 1-2 HAUTEUR=410 mm  [stored 1.34514 ft]; VENTIL_TROU1 LONGUEUR=700 mm  [stored 2.29659 ft]; VENTIL_TROU2 LONGUEUR=700 mm  [stored 2.29659 ft]
- HOSPITAIR C1 - 15 bar - MVB16 (NO CLIM): C1 LONGUEUR=955 mm  [stored 3.1332 ft]; C1-C2_HAUTEUR=1430 mm; C1-C2_HAUTEUR TROU=400 mm  [stored 1.31234 ft]; C1_LONGUEUR TROU=400 mm  [stored 1.31234 ft]; C2 LONGUEUR=1500 mm; C2_LONGUEUR TROU=400 mm  [stored 1.31234 ft]; CLIMATISATION=Non; DESCR_ALIM_X=Alimentation électrique, 5G16mm²; DESCR_ALIM_Y=NE PAS UTILLISER; DESCR_REFOULEMENT RESEAU_AIR=Refoulement Réseau Air; 102m3/h; G3/4"FEM; DESCR_RESERVOIR_AIR=Connexion Réservoir Air; G3/4"FEM; DIAM_REFOULEMENT RESEAU_AIR=20 mm  [stored 0.0656168 ft]; DIAM_RESEVOIR_AIR=20 mm  [stored 0.0656168 ft]; DOUBLE_ALIMENTATION=Non; Debit_refoulement réseau_air=102.0 m³/h; Debit_réservoir_air=102.0 m³/h; ELEC_ALIM Y=Non; HAUT_CONDENSATS=388 mm  [stored 1.27297 ft]; HAUT_SORTIE_RESEAU=1392 mm; HAUT_SORTIE_RESERV=1164 mm; HAUT_TROU_VENTIL=2060 mm; LARG_CONDENSATS=723 mm  [stored 2.37205 ft]; LARG_SORTIE_RESEAU=770 mm  [stored 2.52625 ft]; LARG_SORTIE_RESERV=1530 mm; LONGUEUR_CABINE=2500 mm; MVA9_ASPI_VENT C1=Oui; MVA9_ASPI_VENT C2=Non; MVB12_C1=Oui; MVB12_C2=Non; MVC19-23_ASPI_VENT C1=Non; MVC19-23_ASPI_VENT C2=Non; MVC19-23_C1=Non; MVC19-23_C2=Non; MVX4-5 MVA9_C1=Non; MVX4-5 MVA9_C2=Non; MVX4-5_ASPI_VENT C1=Non; MVX4-5_MVA9_MVB12-16_MVC19-23_VENT=Oui; NIVEAU_SONORE(dB(A))=62; POIDS(Kg)=1600 mm; PUISS_APPARENTE_X=19667 VA; PUISS_APPARENTE_Y=0 VA; PUISS_ELECT_X=18 kW; PUISS_ELECT_Y=0 kW; VENTILATION LONGUEUR=1855 mm; VENTIL_LONGUEUR 1=360 mm  [stored 1.1811 ft]; VENTIL_LONGUEUR 2=2000 mm; VENTIL_TROU 1-2  HAUTEUR=700 mm  [stored 2.29659 ft]; VENTIL_TROU 1-2 HAUTEUR=360 mm  [stored 1.1811 ft]; VENTIL_TROU1 LONGUEUR=700 mm  [stored 2.29659 ft]; VENTIL_TROU2 LONGUEUR=700 mm  [stored 2.29659 ft]
- HOSPITAIR C1 - 15 bar - MVC19 (NO CLIM): C1 LONGUEUR=1247 mm; C1-C2_HAUTEUR=1719 mm; C1-C2_HAUTEUR TROU=500 mm  [stored 1.64042 ft]; C1_LONGUEUR TROU=500 mm  [stored 1.64042 ft]; C2 LONGUEUR=2000 mm; C2_LONGUEUR TROU=500 mm  [stored 1.64042 ft]; CLIMATISATION=Non; DESCR_ALIM_X=Alimentation électrique, 5G25mm²; DESCR_ALIM_Y=NE PAS UTILLISER; DESCR_REFOULEMENT RESEAU_AIR=Refoulement Réseau Air; 150m3/h; G3/4"FEM; DESCR_RESERVOIR_AIR=Connexion Réservoir Air; G3/4"FEM; DIAM_REFOULEMENT RESEAU_AIR=20 mm  [stored 0.0656168 ft]; DIAM_RESEVOIR_AIR=20 mm  [stored 0.0656168 ft]; DOUBLE_ALIMENTATION=Non; Debit_refoulement réseau_air=150.0 m³/h; Debit_réservoir_air=150.0 m³/h; ELEC_ALIM Y=Non; HAUT_CONDENSATS=388 mm  [stored 1.27297 ft]; HAUT_SORTIE_RESEAU=1430 mm; HAUT_SORTIE_RESERV=1105 mm; HAUT_TROU_VENTIL=1960 mm; LARG_CONDENSATS=723 mm  [stored 2.37205 ft]; LARG_SORTIE_RESEAU=938 mm; LARG_SORTIE_RESERV=1765 mm; LONGUEUR_CABINE=3000 mm; MVA9_ASPI_VENT C1=Oui; MVA9_ASPI_VENT C2=Non; MVB12_C1=Non; MVB12_C2=Non; MVC19-23_ASPI_VENT C1=Non; MVC19-23_ASPI_VENT C2=Non; MVC19-23_C1=Oui; MVC19-23_C2=Non; MVX4-5 MVA9_C1=Non; MVX4-5 MVA9_C2=Non; MVX4-5_ASPI_VENT C1=Non; MVX4-5_MVA9_MVB12-16_MVC19-23_VENT=Oui; NIVEAU_SONORE(dB(A))=62; POIDS(Kg)=1670 mm; PUISS_APPARENTE_X=23556 VA; PUISS_APPARENTE_Y=0 VA; PUISS_ELECT_X=21 kW; PUISS_ELECT_Y=0 kW; VENTILATION LONGUEUR=2647 mm; VENTIL_LONGUEUR 1=360 mm  [stored 1.1811 ft]; VENTIL_LONGUEUR 2=2500 mm; VENTIL_TROU 1-2  HAUTEUR=700 mm  [stored 2.29659 ft]; VENTIL_TROU 1-2 HAUTEUR=360 mm  [stored 1.1811 ft]; VENTIL_TROU1 LONGUEUR=700 mm  [stored 2.29659 ft]; VENTIL_TROU2 LONGUEUR=700 mm  [stored 2.29659 ft]
- HOSPITAIR C1 - 15 bar - MVC23 (NO CLIM): C1 LONGUEUR=1247 mm; C1-C2_HAUTEUR=1719 mm; C1-C2_HAUTEUR TROU=500 mm  [stored 1.64042 ft]; C1_LONGUEUR TROU=500 mm  [stored 1.64042 ft]; C2 LONGUEUR=2000 mm; C2_LONGUEUR TROU=500 mm  [stored 1.64042 ft]; CLIMATISATION=Non; DESCR_ALIM_X=Alimentation électrique, 5G25mm²; DESCR_ALIM_Y=NE PAS UTILLISER; DESCR_REFOULEMENT RESEAU_AIR=Refoulement Réseau Air; 174m3/h; G3/4"FEM; DESCR_RESERVOIR_AIR=Connexion Réservoir Air; G3/4"FEM; DIAM_REFOULEMENT RESEAU_AIR=20 mm  [stored 0.0656168 ft]; DIAM_RESEVOIR_AIR=20 mm  [stored 0.0656168 ft]; DOUBLE_ALIMENTATION=Non; Debit_refoulement réseau_air=174.0 m³/h; Debit_réservoir_air=174.0 m³/h; ELEC_ALIM Y=Non; HAUT_CONDENSATS=388 mm  [stored 1.27297 ft]; HAUT_SORTIE_RESEAU=1430 mm; HAUT_SORTIE_RESERV=1106 mm; HAUT_TROU_VENTIL=1960 mm; LARG_CONDENSATS=716 mm  [stored 2.34908 ft]; LARG_SORTIE_RESEAU=938 mm; LARG_SORTIE_RESERV=1765 mm; LONGUEUR_CABINE=3000 mm; MVA9_ASPI_VENT C1=Oui; MVA9_ASPI_VENT C2=Non; MVB12_C1=Non; MVB12_C2=Non; MVC19-23_ASPI_VENT C1=Non; MVC19-23_ASPI_VENT C2=Non; MVC19-23_C1=Oui; MVC19-23_C2=Non; MVX4-5 MVA9_C1=Non; MVX4-5 MVA9_C2=Non; MVX4-5_ASPI_VENT C1=Non; MVX4-5_MVA9_MVB12-16_MVC19-23_VENT=Oui; NIVEAU_SONORE(dB(A))=63; POIDS(Kg)=1950 mm; PUISS_APPARENTE_X=27444 VA; PUISS_APPARENTE_Y=0 VA; PUISS_ELECT_X=25 kW; PUISS_ELECT_Y=0 kW; VENTILATION LONGUEUR=2647 mm; VENTIL_LONGUEUR 1=360 mm  [stored 1.1811 ft]; VENTIL_LONGUEUR 2=3000 mm; VENTIL_TROU 1-2  HAUTEUR=700 mm  [stored 2.29659 ft]; VENTIL_TROU 1-2 HAUTEUR=360 mm  [stored 1.1811 ft]; VENTIL_TROU1 LONGUEUR=700 mm  [stored 2.29659 ft]; VENTIL_TROU2 LONGUEUR=700 mm  [stored 2.29659 ft]
- HOSPITAIR C1 - 15 bar - MVX5 (NO CLIM): C1 LONGUEUR=905 mm  [stored 2.96916 ft]; C1-C2_HAUTEUR=1146.5 mm; C1-C2_HAUTEUR TROU=300 mm  [stored 0.984252 ft]; C1_LONGUEUR TROU=300 mm  [stored 0.984252 ft]; C2 LONGUEUR=1200 mm; C2_LONGUEUR TROU=300 mm  [stored 0.984252 ft]; CLIMATISATION=Non; DESCR_ALIM_X=Alimentation électrique, 5G4mm²; DESCR_ALIM_Y=NE PAS UTILLISER; DESCR_REFOULEMENT RESEAU_AIR=Refoulement Réseau Air; 32m3/h; G1/2"FEM; DESCR_RESERVOIR_AIR=Connexion Réservoir Air; G1/2"FEM; DIAM_REFOULEMENT RESEAU_AIR=15 mm  [stored 0.0492126 ft]; DIAM_RESEVOIR_AIR=15 mm  [stored 0.0492126 ft]; DOUBLE_ALIMENTATION=Non; Debit_refoulement réseau_air=32.0 m³/h; Debit_réservoir_air=32.0 m³/h; ELEC_ALIM Y=Non; HAUT_CONDENSATS=310 mm  [stored 1.01706 ft]; HAUT_SORTIE_RESEAU=1608 mm; HAUT_SORTIE_RESERV=1260 mm; HAUT_TROU_VENTIL=2041.5 mm; LARG_CONDENSATS=785 mm; LARG_SORTIE_RESEAU=775 mm  [stored 2.54265 ft]; LARG_SORTIE_RESERV=1457 mm; LONGUEUR_CABINE=2200 mm; MVA9_ASPI_VENT C1=Non; MVA9_ASPI_VENT C2=Non; MVB12_C1=Non; MVB12_C2=Non; MVC19-23_ASPI_VENT C1=Non; MVC19-23_ASPI_VENT C2=Non; MVC19-23_C1=Non; MVC19-23_C2=Non; MVX4-5 MVA9_C1=Oui; MVX4-5 MVA9_C2=Non; MVX4-5_ASPI_VENT C1=Oui; MVX4-5_MVA9_MVB12-16_MVC19-23_VENT=Oui; NIVEAU_SONORE(dB(A))=57; POIDS(Kg)=1070 mm; PUISS_APPARENTE_X=9111 VA; PUISS_APPARENTE_Y=0 VA; PUISS_ELECT_X=8 kW; PUISS_ELECT_Y=0 kW; VENTILATION LONGUEUR=1595 mm; VENTIL_LONGUEUR 1=360 mm  [stored 1.1811 ft]; VENTIL_LONGUEUR 2=2000 mm; VENTIL_TROU 1-2  HAUTEUR=500 mm  [stored 1.64042 ft]; VENTIL_TROU 1-2 HAUTEUR=360 mm  [stored 1.1811 ft]; VENTIL_TROU1 LONGUEUR=500 mm  [stored 1.64042 ft]; VENTIL_TROU2 LONGUEUR=500 mm  [stored 1.64042 ft]
- HOSPITAIR C2 - 15 bar - MVX5 (CLIM): C1 LONGUEUR=910 mm  [stored 2.98556 ft]; C1-C2_HAUTEUR=1145 mm; C1-C2_HAUTEUR TROU=300 mm  [stored 0.984252 ft]; C1_LONGUEUR TROU=300 mm  [stored 0.984252 ft]; C2 LONGUEUR=970 mm; C2_LONGUEUR TROU=300 mm  [stored 0.984252 ft]; CLIMATISATION=Oui; DESCR_ALIM_X=Alimentation électrique, 5G4mm²; DESCR_ALIM_Y=Alimentation électrique, 5G2.5mm²; DESCR_REFOULEMENT RESEAU_AIR=Refoulement Réseau Air; 44m3/h; G3/4"FEM; DESCR_RESERVOIR_AIR=Connexion Réservoir Air; G3/4"FEM; DIAM_REFOULEMENT RESEAU_AIR=20 mm  [stored 0.0656168 ft]; DIAM_RESEVOIR_AIR=20 mm  [stored 0.0656168 ft]; DOUBLE_ALIMENTATION=Oui; Debit_refoulement réseau_air=44.0 m³/h; Debit_réservoir_air=44.0 m³/h; ELEC_ALIM Y=Oui; HAUT_CONDENSATS=308 mm  [stored 1.0105 ft]; HAUT_SORTIE_RESEAU=1498 mm; HAUT_SORTIE_RESERV=1216 mm; HAUT_TROU_VENTIL=2041.5 mm; LARG_CONDENSATS=857 mm  [stored 2.81168 ft]; LARG_SORTIE_RESEAU=785 mm; LARG_SORTIE_RESERV=1580 mm; LONGUEUR_CABINE=3500 mm; MVA9_ASPI_VENT C1=Non; MVA9_ASPI_VENT C2=Non; MVB12_C1=Non; MVB12_C2=Non; MVC19-23_ASPI_VENT C1=Non; MVC19-23_ASPI_VENT C2=Non; MVC19-23_C1=Non; MVC19-23_C2=Non; MVX4-5 MVA9_C1=Oui; MVX4-5 MVA9_C2=Oui; MVX4-5_ASPI_VENT C1=Oui; MVX4-5_MVA9_MVB12-16_MVC19-23_VENT=Non; NIVEAU_SONORE(dB(A))=57; POIDS(Kg)=1880 mm; PUISS_APPARENTE_X=11000 VA; PUISS_APPARENTE_Y=6222 VA; PUISS_ELECT_X=10 kW; PUISS_ELECT_Y=6 kW; VENTILATION LONGUEUR=4500 mm; VENTIL_LONGUEUR 1=450 mm  [stored 1.47638 ft]; VENTIL_LONGUEUR 2=3000 mm; VENTIL_TROU 1-2  HAUTEUR=600 mm  [stored 1.9685 ft]; VENTIL_TROU 1-2 HAUTEUR=360 mm  [stored 1.1811 ft]; VENTIL_TROU1 LONGUEUR=600 mm  [stored 1.9685 ft]; VENTIL_TROU2 LONGUEUR=500 mm  [stored 1.64042 ft]
- HOSPITAIR C2 - 15 bar - MVX5 (NO CLIM): C1 LONGUEUR=910 mm  [stored 2.98556 ft]; C1-C2_HAUTEUR=1145 mm; C1-C2_HAUTEUR TROU=300 mm  [stored 0.984252 ft]; C1_LONGUEUR TROU=300 mm  [stored 0.984252 ft]; C2 LONGUEUR=970 mm; C2_LONGUEUR TROU=300 mm  [stored 0.984252 ft]; CLIMATISATION=Non; DESCR_ALIM_X=Alimentation électrique, 5G4mm²; DESCR_ALIM_Y=Alimentation électrique, 5G2.5mm²; DESCR_REFOULEMENT RESEAU_AIR=Refoulement Réseau Air; 44m3/h; G3/4"FEM; DESCR_RESERVOIR_AIR=Connexion Réservoir Air; G3/4"FEM; DIAM_REFOULEMENT RESEAU_AIR=20 mm  [stored 0.0656168 ft]; DIAM_RESEVOIR_AIR=20 mm  [stored 0.0656168 ft]; DOUBLE_ALIMENTATION=Oui; Debit_refoulement réseau_air=44.0 m³/h; Debit_réservoir_air=44.0 m³/h; ELEC_ALIM Y=Oui; HAUT_CONDENSATS=310 mm  [stored 1.01706 ft]; HAUT_SORTIE_RESEAU=1510 mm; HAUT_SORTIE_RESERV=1200 mm; HAUT_TROU_VENTIL=2000 mm; LARG_CONDENSATS=1100 mm; LARG_SORTIE_RESEAU=785 mm; LARG_SORTIE_RESERV=1580 mm; LONGUEUR_CABINE=3500 mm; MVA9_ASPI_VENT C1=Non; MVA9_ASPI_VENT C2=Non; MVB12_C1=Non; MVB12_C2=Non; MVC19-23_ASPI_VENT C1=Non; MVC19-23_ASPI_VENT C2=Non; MVC19-23_C1=Non; MVC19-23_C2=Non; MVX4-5 MVA9_C1=Oui; MVX4-5 MVA9_C2=Oui; MVX4-5_ASPI_VENT C1=Oui; MVX4-5_MVA9_MVB12-16_MVC19-23_VENT=Oui; NIVEAU_SONORE(dB(A))=57; POIDS(Kg)=1880 mm; PUISS_APPARENTE_X=9111 VA; PUISS_APPARENTE_Y=6222 VA; PUISS_ELECT_X=8 kW; PUISS_ELECT_Y=6 kW; VENTILATION LONGUEUR=2940 mm; VENTIL_LONGUEUR 1=450 mm  [stored 1.47638 ft]; VENTIL_LONGUEUR 2=3000 mm; VENTIL_TROU 1-2  HAUTEUR=500 mm  [stored 1.64042 ft]; VENTIL_TROU 1-2 HAUTEUR=360 mm  [stored 1.1811 ft]; VENTIL_TROU1 LONGUEUR=600 mm  [stored 1.9685 ft]; VENTIL_TROU2 LONGUEUR=500 mm  [stored 1.64042 ft]

note: [stored X ft] marks values corroborated as IEEE doubles in the binary element streams (Revit-internal decimal feet)
